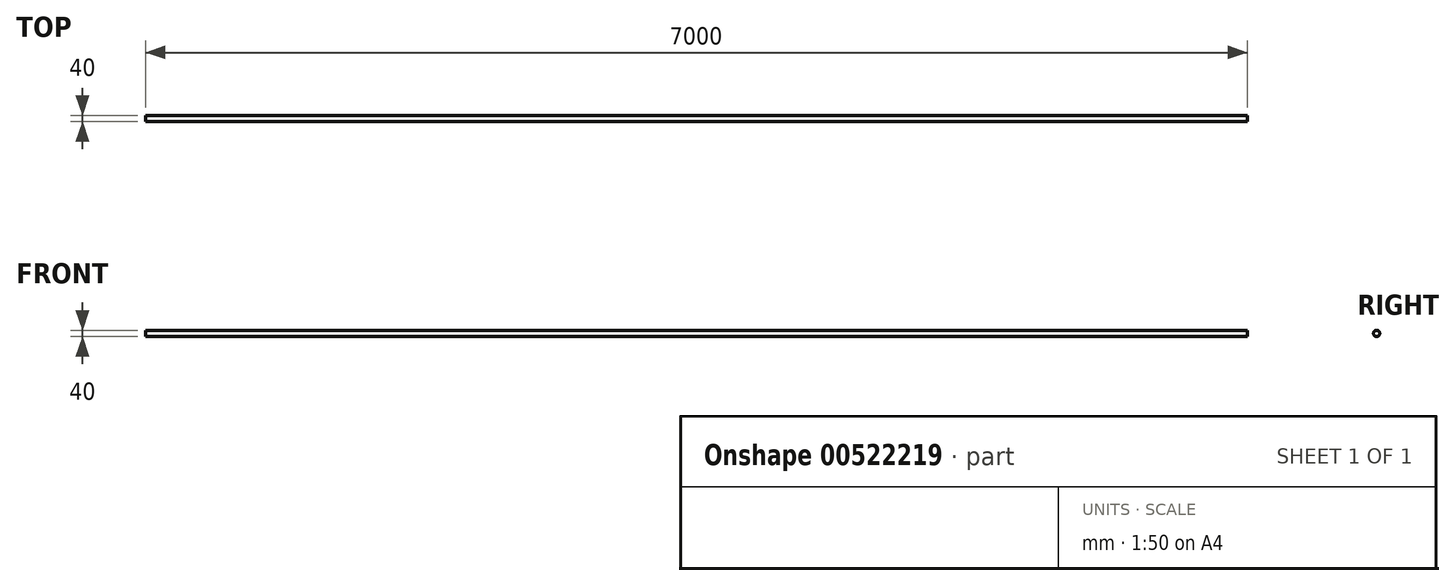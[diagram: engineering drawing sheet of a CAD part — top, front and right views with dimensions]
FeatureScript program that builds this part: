
annotation { "Feature Type Name" : "Feature", "Feature Type Description" : "" }
export const myFeature = defineFeature(function(context is Context, id is Id, definition is map)
    precondition{}
    {
        {
            var Q0;
            Q0=qCreatedBy(makeId("Right.planeOp"),FACE);
            var sketch = newSketch(context, id + "F0", { "sketchPlane" : qUnion([Q0])});
            skCircle(sketch, "E0", {"center": v(0, 0) * mm, "radius": 20 * mm});
            skSolve(sketch);
        }
        {
            var Q0;
            Q0 = qSketchRegion(id + "F0", true);
            extrude(context, id + "F1", {"entities" : qUnion([Q0]), "depth" : 7000 * mm, "offsetDistance" : 25 * mm});
        }
    });
